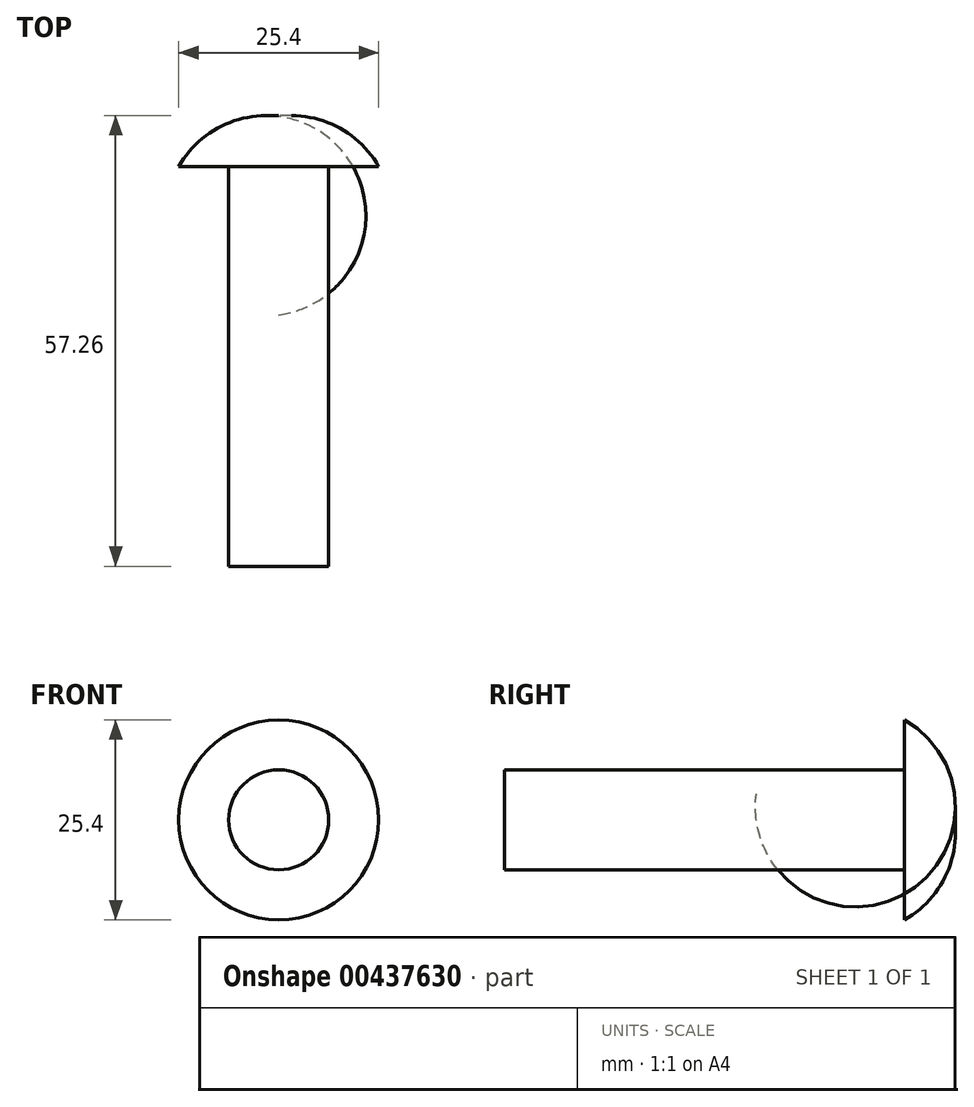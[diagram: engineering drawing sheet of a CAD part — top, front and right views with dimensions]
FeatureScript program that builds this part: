
annotation { "Feature Type Name" : "Feature", "Feature Type Description" : "" }
export const myFeature = defineFeature(function(context is Context, id is Id, definition is map)
    precondition{}
    {
        {
            var Q0;
            Q0=qCreatedBy(makeId("Front.planeOp"),FACE);
            var sketch = newSketch(context, id + "F0", { "sketchPlane" : qUnion([Q0])});
            skCircle(sketch, "E0", {"center": v(0, 0) * mm, "radius": 6.35 * mm});
            skSolve(sketch);
        }
        {
            var Q0;
            Q0 = qSketchRegion(id + "F0", true);
            extrude(context, id + "F1", {"entities" : qUnion([Q0]), "depth" : 50.8 * mm});
        }
        {
            var Q0;
            Q0=qCreatedBy(makeId("Top.planeOp"),FACE);
            var sketch = newSketch(context, id + "F2", { "sketchPlane" : qUnion([Q0])});
            skLineSegment(sketch, "E1", {"start": v(0, 0) * mm, "end": v(12.7, 0) * mm});
            skArc(sketch, "E2", {"start": v(12.7, 0) * mm, "mid": v(7.32, 5.12) * mm, "end": v(0, 6.35) * mm});
            skLineSegment(sketch, "E3", {"start": v(0, 6.35) * mm, "end": v(0, 0) * mm});
            skSolve(sketch);
        }
        {
            var Q0;
            Q0 = qSketchRegion(id + "F2", true);
            var Q1;
            Q1=sQuery(id+"F2.wireOp",EDGE,"E3");
            revolve(context, id + "F3", {"operationType" : NewBodyOperationType.ADD, "entities" : qUnion([Q0]), "axis" : qUnion([Q1]), "revolveType" : RevolveType.FULL});
        }
    });
